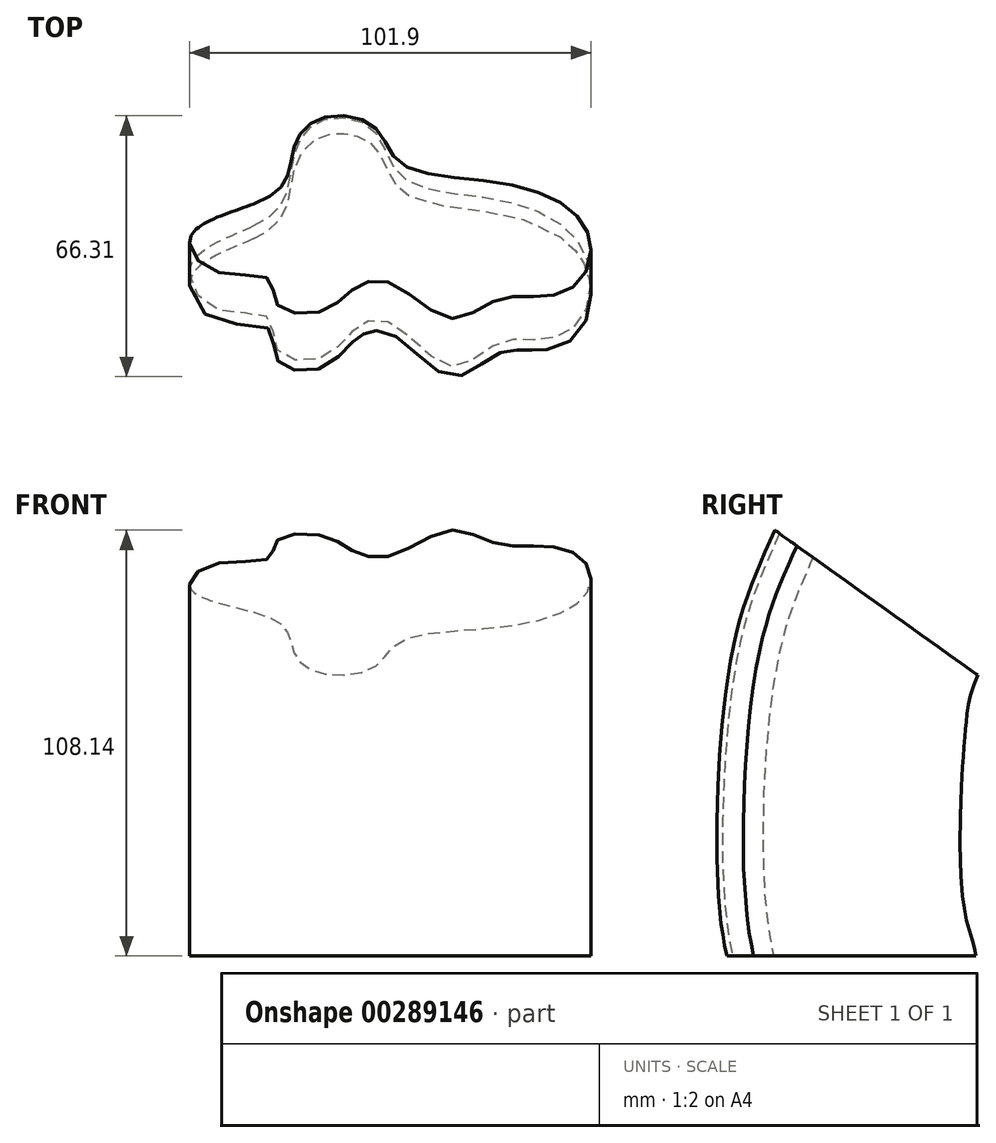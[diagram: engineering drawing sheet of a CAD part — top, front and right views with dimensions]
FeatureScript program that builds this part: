
annotation { "Feature Type Name" : "Feature", "Feature Type Description" : "" }
export const myFeature = defineFeature(function(context is Context, id is Id, definition is map)
    precondition{}
    {
        {
            var Q0;
            Q0=qCreatedBy(makeId("Top.planeOp"),FACE);
            var sketch = newSketch(context, id + "F0", { "sketchPlane" : qUnion([Q0])});
            skFitSpline(sketch, "E0", {"points": [v(-43.82, 7.14) * mm, v(-35.74, 14.5) * mm, v(-33.05, 26.54) * mm, v(-26.04, 34.08) * mm, v(-13.47, 31.57) * mm, v(-6.1, 19.53) * mm, v(21, 13.23) * mm, v(40.4, 0) * mm, v(38.97, -17.13) * mm, v(28.91, -21.8) * mm, v(18.32, -22.7) * mm, v(6.46, -28.62) * mm, v(-8.44, -17.84) * mm, v(-17.42, -18.56) * mm, v(-26.22, -26.28) * mm, v(-37.72, -24.48) * mm, v(-39.87, -16.4) * mm, v(-53.7, -13.88) * mm, v(-59.63, -2.74) * mm, v(-43.82, 7.14) * mm]});
            skSolve(sketch);
        }
        {
            var Q0;
            Q0=qCreatedBy(makeId("Right.planeOp"),FACE);
            var sketch = newSketch(context, id + "F1", { "sketchPlane" : qUnion([Q0])});
            skFitSpline(sketch, "E1", {"points": [v(0, 0) * mm, v(-2.86, 19.37) * mm, v(0, 69.98) * mm, v(6.9, 91.48) * mm], "startDerivative": vector(-13.04, 59.27) * mm, "endDerivative": vector(26.25, 61.43) * mm});
            skSolve(sketch);
        }
        {
            var Q0;
            Q0=makeQuery(id+"F0.imprint","IMPRINT",FACE,{"disambiguationData":[TD([[makeQuery(id+"F0.imprint","IMPRINT",EDGE,{"derivedFrom":sQuery(id+"F0.wireOp",EDGE,"E0")}),-1.0]])]});
            var Q1;
            Q1=sQuery(id+"F1.wireOp",EDGE,"E1");
            sweep(context, id + "F2", {"profiles" : qUnion([Q0]), "path" : qUnion([Q1])});
        }
    });
